# Revit family: Lil_F
name_source: partatom
category: Plumbing Fixtures
units: mm (PartAtom-declared; Revit-internal decimal feet)

## family parameters
Always vertical = Yes
Cut with Voids When Loaded = No
Part Type = Normal
Room Calculation Point = No
Round Connector Dimension = Use Diameter
Shared = No
Work Plane-Based = No

## types (7) — shared parameters
BOTTOM 1 = 9"
FULL DIM = 6"
Manufacturer = MIFAB
Material = Polyethylene, High Density
Pressure Drop = 0.00 psi
TOP THK = 1 1/2"
TOP1 = 1 1/2"
URL = www.mifab.com

## per-type parameters (varying)
| type | A | A+1 | B | C | D | Description | E | F | F/2 | F2 | Mechanical Flow | Model | top 2 |
| Lil-7-F | 19 1/2" | 10 1/2" | 15 1/2" | 3 1/2" | 9" | 7GPM Lil Max Fish Scale Interceptor | 12 1/2" | 2" | 1" | 13/16" | 7 GPM | MI-G-1-PL-PSB-FSCR | 2" |
| Lil-10-F | 23" | 12 5/16" | 17 1/2" | 3 1/2" | 9 3/4" | 10GPM Lil Max Fish Scale Interceptor | 13 1/4" | 2" | 1" | 13/16" | 10 GPM | MI-G-2-PL-PSB-FSCR | 3 1/8" |
| Lil-15-F | 23" | 12 5/16" | 17 1/2" | 3 1/2" | 13 1/4" | 15GPM Lil Max Fish Scale Interceptor | 16 3/4" | 2" | 1" | 13/16" | 15 GPM | MI-G-3-PL-PSB-FSCR | 3 1/8" |
| Lil-20-F | 29 1/2" | 15 5/8" | 20 1/2" | 3 1/2" | 10 3/4" | 20GPM Lil Max Fish Scale Interceptor | 14 1/4" | 3" | 1 1/2" | 1 5/16" | 20 GPM | MI-G-4-PL-PSB-FSCR | 3 1/8" |
| Lil-25-F | 29 1/2" | 15 5/8" | 20 1/2" | 3 1/2" | 14 3/4" | 25GPM Lil Max Fish Scale Interceptor | 18 1/4" | 3" | 1 1/2" | 1 5/16" | 25 GPM | MI-G-5-PL-PSB-FSCR | 3 1/8" |
| Lil-35-F | 33" | 17 7/16" | 25 1/2" | 5 1/2" | 16 3/4" | 35GPM Lil Max Fish Scale Interceptor | 22 1/4" | 3" | 1 1/2" | 1 5/16" | 35 GPM | MI-G-6-PL-PSB-FSCR | 3 1/8" |
| Lil-50-F | 33" | 17 7/16" | 25 1/2" | 5 1/2" | 18 3/4" | 50GPM Lil Max Fish Scale Interceptor | 24 1/4" | 3" | 1 1/2" | 1 5/16" | 50 GPM | MI-G-7-PL-PSB-FSCR | 3 1/8" |

## geometry (parser evidence)
native form markers: Sweep x2
no freeform markers — native parametric forms only
